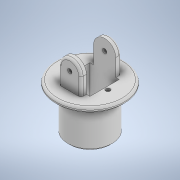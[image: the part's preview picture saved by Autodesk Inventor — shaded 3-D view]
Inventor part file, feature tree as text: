
AUTODESK INVENTOR PART (.ipt)
format: ipt  version: 2022 (Build 260153000, 153)  size: 212,480 bytes
history: native  units: in
note: dims shown in document units (in); Inventor stores cm internally (conversion verified against a paired STEP export)
features: extrude x6, sketch x6, chamfer x2, fillet x2
ambient origin geometry x8: Origin, YZ Plane, XZ Plane, XY Plane, X Axis, Y Axis, Z Axis, Center Point
bodies: Solid1 (feature_tree)
feature tree (16):
  extrude  "Extrusion1"  Depth=1.4567in TaperAngle=0.0deg
  extrude  "Extrusion2"  Depth=0.1969in TaperAngle=0.0deg
  chamfer  "Chamfer1"  Distance=0.0787in Angle=45.0deg
  extrude  "Extrusion3"  Depth=1.0394in
  extrude  "Extrusion4"  Depth=0.1575in
  extrude  "Extrusion5"  Depth=0.7874in TaperAngle=0.0deg
  fillet  "Fillet1"  Radius=0.7874in
  extrude  "Extrusion6"  Depth=0.7874in
  fillet  "Fillet2"  Radius=0.1969in
  chamfer  "Chamfer2"  Distance=1.0079in
  sketch  "Sketch1"  dims[d0=1.5748in d1=1.4567in d2=0.0in]
  sketch  "Sketch2"  dims[d3=2.4409in d4=0.1969in d5=0.0in d6=0.0787in d7=0.0787in d8=45.0deg]
  sketch  "Sketch3"  dims[d9=1.0394in d10=1.0394in]
  sketch  "Sketch4"  dims[d11=1.9685in d12=0.0in d13=0.1575in]
  sketch  "Sketch5"  dims[d14=0.1575in d15=1.9685in d16=0.0in d17=0.7874in]
  sketch  "Sketch6"  dims[d18=0.1969in d19=0.7874in d20=0.1969in d21=1.0079in d22=0.0in d23=0.3937in d24=0.1575in d25=1.9685in d26=0.0in d27=0.0787in d28=0.0787in d29=0.0787in d30=45.0deg d31=0.6142in]
